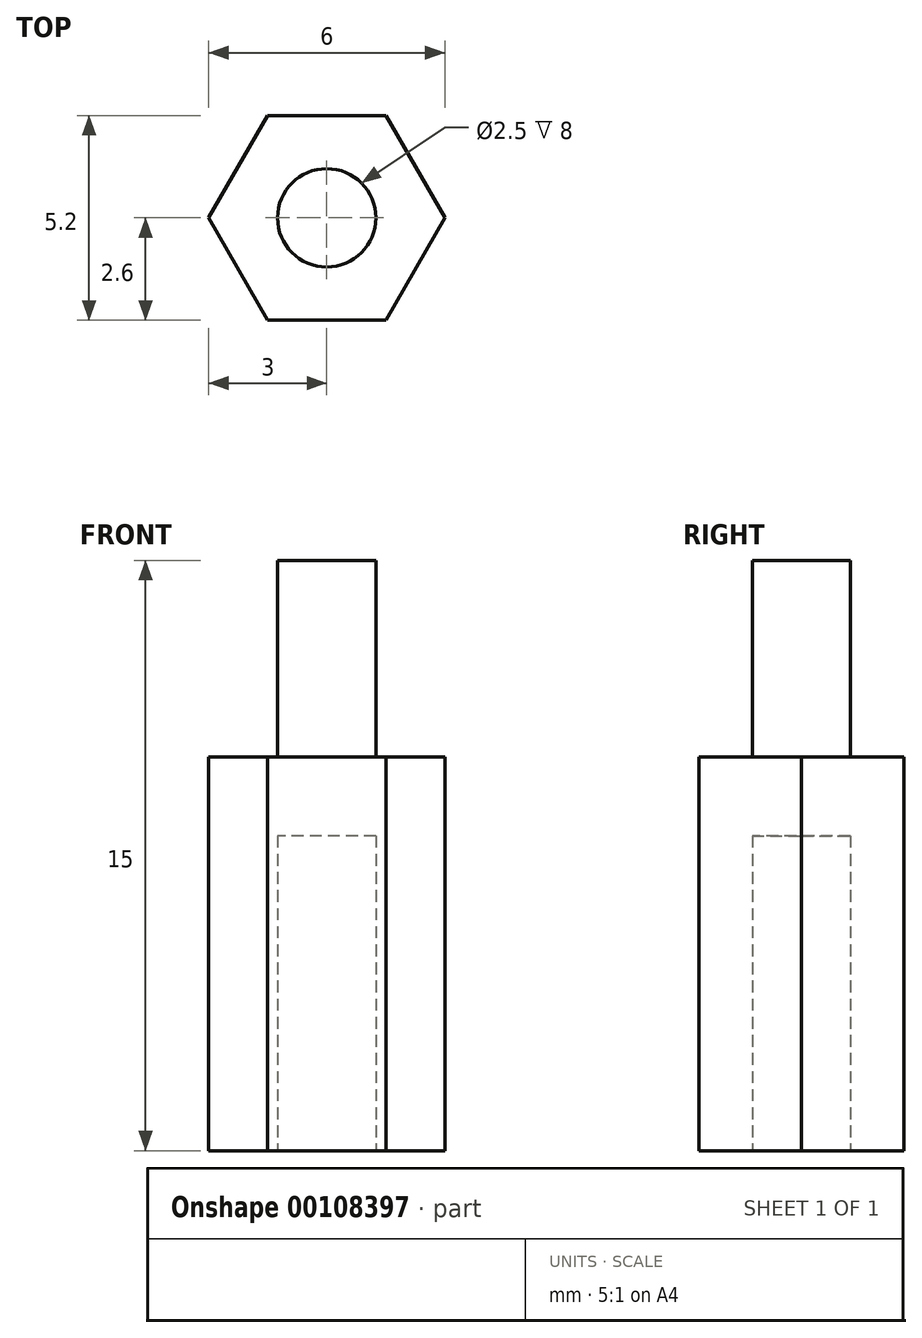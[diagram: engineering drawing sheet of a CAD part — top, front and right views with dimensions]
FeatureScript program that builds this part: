
annotation { "Feature Type Name" : "Feature", "Feature Type Description" : "" }
export const myFeature = defineFeature(function(context is Context, id is Id, definition is map)
    precondition{}
    {
        {
            var Q0;
            Q0=qCreatedBy(makeId("Top.planeOp"),FACE);
            var sketch = newSketch(context, id + "F0", { "sketchPlane" : qUnion([Q0])});
            skCircle(sketch, "E0.cCircle", {"center": v(0, 0) * mm, "radius": 2.6 * mm, "construction": true});
            skLineSegment(sketch, "E0.0", {"start": v(-1.5, 2.6) * mm, "end": v(1.5, 2.6) * mm});
            skLineSegment(sketch, "E0.1", {"start": v(1.5, 2.6) * mm, "end": v(3, 0) * mm});
            skLineSegment(sketch, "E0.2", {"start": v(3, 0) * mm, "end": v(1.5, -2.6) * mm});
            skLineSegment(sketch, "E0.3", {"start": v(1.5, -2.6) * mm, "end": v(-1.5, -2.6) * mm});
            skLineSegment(sketch, "E0.4", {"start": v(-1.5, -2.6) * mm, "end": v(-3, 0) * mm});
            skLineSegment(sketch, "E0.5", {"start": v(-3, 0) * mm, "end": v(-1.5, 2.6) * mm});
            skPoint(sketch, "E0.0.midPoint", {"position": v(0, 2.6) * mm});
            skCircle(sketch, "E1", {"center": v(0, 0) * mm, "radius": 1.25 * mm});
            skSolve(sketch);
        }
        {
            var Q0;
            Q0=makeQuery(id+"F0.imprint","IMPRINT",FACE,{"disambiguationData":[TD([[makeQuery(id+"F0.imprint","IMPRINT",EDGE,{"derivedFrom":sQuery(id+"F0.wireOp",EDGE,"E0.0")}),-1.0]])]});
            extrude(context, id + "F1", {"entities" : qUnion([Q0]), "depth" : 10 * mm});
        }
        {
            var Q0;
            Q0=makeQuery(id+"F0.imprint","IMPRINT",FACE,{"disambiguationData":[TD([[makeQuery(id+"F0.imprint","IMPRINT",EDGE,{"derivedFrom":sQuery(id+"F0.wireOp",EDGE,"E1")}),1.0]])]});
            extrude(context, id + "F2", {"entities" : qUnion([Q0]), "operationType" : NewBodyOperationType.ADD, "depth" : 15 * mm});
        }
        {
            var Q0;
            Q0=makeQuery(id+"F0.imprint","IMPRINT",FACE,{"disambiguationData":[TD([[makeQuery(id+"F0.imprint","IMPRINT",EDGE,{"derivedFrom":sQuery(id+"F0.wireOp",EDGE,"E1")}),1.0]])]});
            extrude(context, id + "F3", {"entities" : qUnion([Q0]), "operationType" : NewBodyOperationType.REMOVE, "depth" : 8 * mm});
        }
    });
